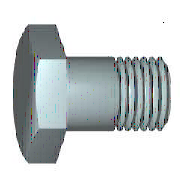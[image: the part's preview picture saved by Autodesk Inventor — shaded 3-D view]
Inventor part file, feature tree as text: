
AUTODESK INVENTOR PART (.ipt)
format: ipt  version: 2020 (Build 240168000, 168)  size: 275,456 bytes
history: native  units: mm (DEFAULTED — no unit token found)
features: sketch x6, plane x3, extrude x3, chamfer x2, other x1, thread x1, revolve x1, fillet x1, projected_geometry x1
ambient origin geometry x7: Origin, YZ Plane, XZ Plane, X Axis, Y Axis, Z Axis, Center Point
bodies: Solid1 (feature_tree)
feature tree (19):
  sketch  "草图1"  dims[d0=35.0mm d1=32.5mm]
  plane  "工作平面3"
  extrude  "头"  Depth=32.5mm
  chamfer  "倒角1"  Distance=0.8001mm
  plane  "Work Plane1"
  plane  "工作平面2"
  other  "分割1"
  extrude  "拉伸5"  Depth=2.0mm
  extrude  "拉伸6"  Depth=2.0mm
  thread  "螺纹3"  [1 undecoded]
  chamfer  "倒角2"  Distance=18.0mm
  revolve  "旋转3"  [1 undecoded]
  fillet  "圆角2"  [1 undecoded]
  sketch  "草图2"  dims[d2=18.0mm]
  sketch  "草图4"  dims[d3=10.7mm]
  sketch  "草图7"  dims[d4=0.0mm]
  sketch  "草图8"  dims[d5=30.0deg]
  sketch  "草图9"  dims[d21=90.0deg d9=0.8001mm d10=25.5mm d11=27.0mm d13=1.533725mm d14=18.0mm d19=27.0mm d58=0.0mm d60=14.0mm d61=1.0mm d62=0.0mm d63=18.0mm d64=11.0mm d65=0.0mm d66=20.0mm d67=0.0mm d68=1.5mm d69=2.0mm d70=45.0deg d71=16.0mm d72=40.0mm d73=1.0mm d74=1.0mm d75=1.0mm d76=1.0mm d77=1.0mm d78=1.0mm d79=1.0mm d80=1.0mm d81=6.0mm d82=2.0mm d83=60.0mm d84=3.5mm d85=90.0deg d86=2.0mm]
  projected_geometry  "投影回路1"
note: 3 required parameter values undecoded (feature->parameter linkage not recoverable at this tier; creation-order binding heuristic only, values carry confidence <= 0.55)